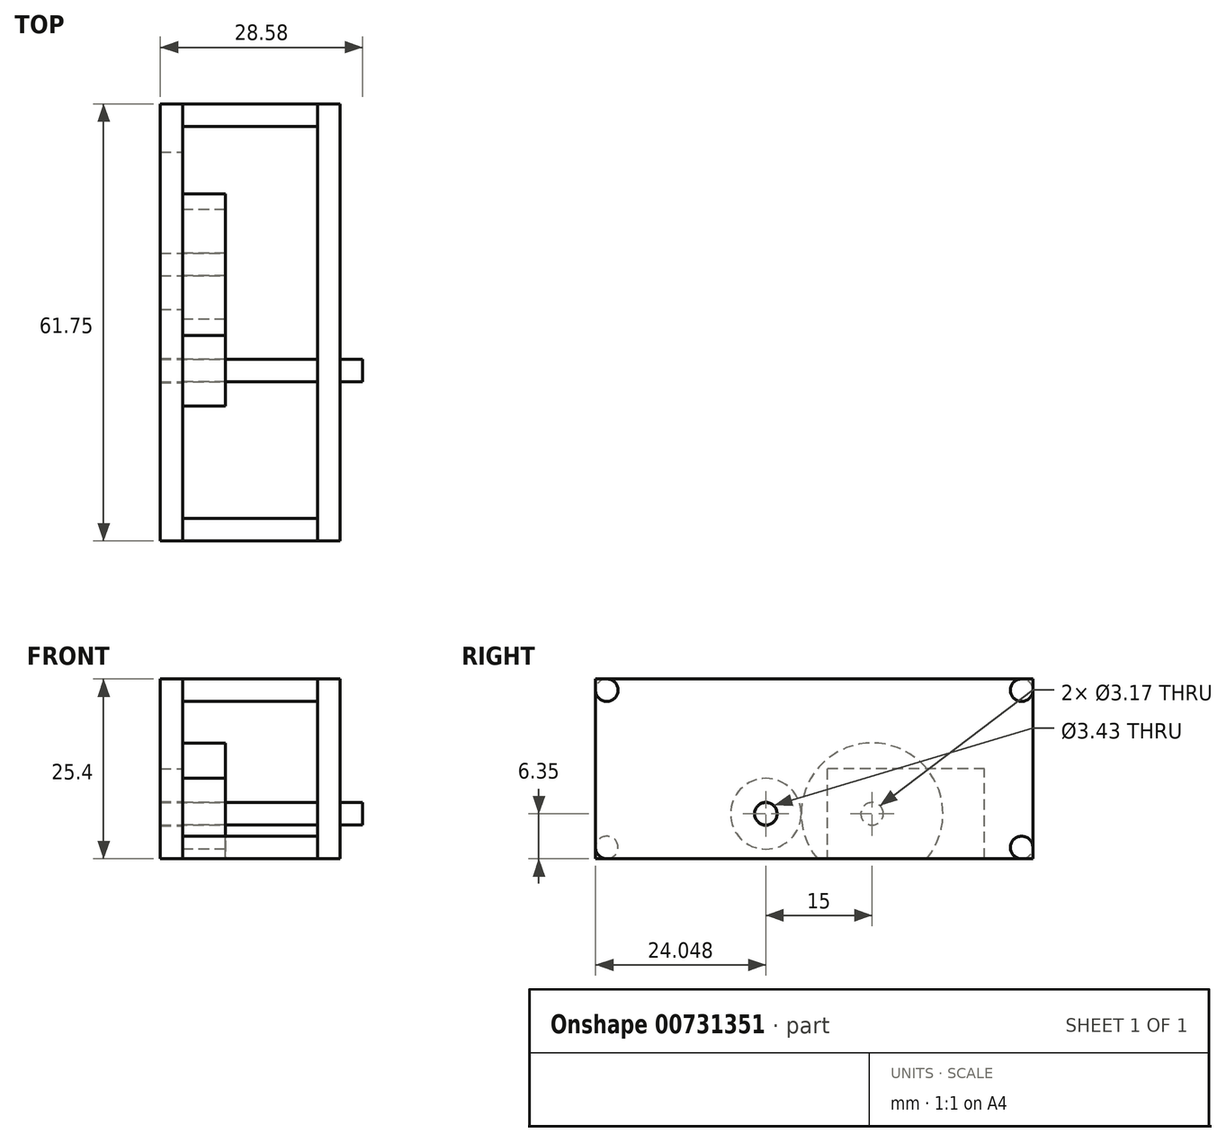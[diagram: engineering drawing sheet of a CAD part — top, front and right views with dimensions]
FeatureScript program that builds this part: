
annotation { "Feature Type Name" : "Feature", "Feature Type Description" : "" }
export const myFeature = defineFeature(function(context is Context, id is Id, definition is map)
    precondition{}
    {
        {
            var Q0;
            Q0=qCreatedBy(makeId("Right.planeOp"),FACE);
            var sketch = newSketch(context, id + "F0", { "sketchPlane" : qUnion([Q0])});
            skLineSegment(sketch, "E0", {"start": v(22.06, 6.35) * mm, "end": v(28.4, 6.35) * mm, "construction": true});
            skCircle(sketch, "E1", {"center": v(28.4, 6.35) * mm, "radius": 10 * mm});
            skLineSegment(sketch, "E2", {"start": v(28.4, 6.35) * mm, "end": v(13.4, 6.35) * mm, "construction": true});
            skCircle(sketch, "E3", {"center": v(13.4, 6.35) * mm, "radius": 5 * mm});
            skCircle(sketch, "E4", {"center": v(13.4, 6.35) * mm, "radius": 1.59 * mm});
            skCircle(sketch, "E5", {"center": v(28.4, 6.35) * mm, "radius": 1.59 * mm});
            skCircle(sketch, "E6", {"center": v(28.4, 6.35) * mm, "radius": 1.84 * mm});
            skLineSegment(sketch, "E7.bottom", {"start": v(35.82, 25.4) * mm, "end": v(51.1, 25.4) * mm});
            skLineSegment(sketch, "E7.top", {"start": v(43.49, 0) * mm, "end": v(51.1, 0) * mm});
            skLineSegment(sketch, "E7.right", {"start": v(51.1, 25.4) * mm, "end": v(51.1, 0) * mm});
            skLineSegment(sketch, "E8", {"start": v(8.4, 6.35) * mm, "end": v(-10.64, 6.35) * mm, "construction": true});
            skLineSegment(sketch, "E9", {"start": v(-10.64, 0) * mm, "end": v(-10.64, 25.4) * mm});
            skCircle(sketch, "E10", {"center": v(-9.05, 23.81) * mm, "radius": 1.59 * mm});
            skPoint(sketch, "E10.first.point", {"position": v(-9.05, 25.4) * mm});
            skPoint(sketch, "E10.second.point", {"position": v(-10.64, 23.81) * mm});
            skPoint(sketch, "E10.third.point", {"position": v(-8.61, 22.29) * mm});
            skCircle(sketch, "E11", {"center": v(-9.05, 1.59) * mm, "radius": 1.59 * mm});
            skPoint(sketch, "E11.first.point", {"position": v(-10.64, 1.59) * mm});
            skPoint(sketch, "E11.second.point", {"position": v(-9.05, 0) * mm});
            skPoint(sketch, "E11.third.point", {"position": v(-8.12, 2.87) * mm});
            skCircle(sketch, "E12", {"center": v(49.52, 1.59) * mm, "radius": 1.59 * mm});
            skPoint(sketch, "E12.first.point", {"position": v(49.52, 0) * mm});
            skPoint(sketch, "E12.second.point", {"position": v(51.1, 1.59) * mm});
            skPoint(sketch, "E12.third.point", {"position": v(47.96, 1.9) * mm});
            skCircle(sketch, "E13", {"center": v(49.52, 23.81) * mm, "radius": 1.59 * mm});
            skPoint(sketch, "E13.first.point", {"position": v(49.52, 25.4) * mm});
            skPoint(sketch, "E13.second.point", {"position": v(51.1, 23.81) * mm});
            skPoint(sketch, "E13.third.point", {"position": v(47.97, 23.48) * mm});
            skLineSegment(sketch, "E14.bottom", {"start": v(35.82, 25.4) * mm, "end": v(41.82, 25.4) * mm});
            skLineSegment(sketch, "E14.top", {"start": v(44.28, 0) * mm, "end": v(50.28, 0) * mm});
            skLineSegment(sketch, "E15", {"start": v(-10.64, 25.4) * mm, "end": v(35.82, 25.4) * mm});
            skLineSegment(sketch, "E16", {"start": v(44.28, 0) * mm, "end": v(44.28, 12.7) * mm});
            skLineSegment(sketch, "E17", {"start": v(44.28, 12.7) * mm, "end": v(22.06, 12.7) * mm});
            skPoint(sketch, "E17.endSnap0", {"position": v(22.06, 3.17) * mm});
            skLineSegment(sketch, "E18", {"start": v(22.06, 12.7) * mm, "end": v(22.06, 0) * mm});
            skLineSegment(sketch, "E19", {"start": v(-10.64, 0) * mm, "end": v(51.1, 0) * mm});
            skSolve(sketch);
        }
        {
            var Q0;
            {var subQ7=sQuery(id+"F0.wireOp",EDGE,"E3");Q0=makeQuery(id+"F0.imprint","IMPRINT",FACE,{"disambiguationData":[TD([[makeQuery(id+"F0.imprint","IMPRINT",EDGE,{"derivedFrom":subQ7}),-1.0]])]});}
            var Q1;
            {var subQ0=sQuery(id+"F0.wireOp",EDGE,"E7.right");var subQ1=sQuery(id+"F0.wireOp",EDGE,"E7.bottom");var subQ2=makeQuery(id+"F0.imprint","INTERSECT",VERTEX,{"derivedFrom":[subQ1,subQ0]});Q1=makeQuery(id+"F0.imprint","IMPRINT",FACE,{"disambiguationData":[TD([[makeQuery(id+"F0.imprint","IMPRINT",EDGE,{"disambiguationData":[TD([[subQ2,1.0]])],"derivedFrom":subQ1}),-1.0]])]});}
            var Q2;
            {var subQ0=sQuery(id+"F0.wireOp",EDGE,"E7.right");var subQ1=sQuery(id+"F0.wireOp",EDGE,"E7.top");var subQ2=makeQuery(id+"F0.imprint","INTERSECT",VERTEX,{"derivedFrom":[subQ1,subQ0]});Q2=makeQuery(id+"F0.imprint","IMPRINT",FACE,{"disambiguationData":[TD([[makeQuery(id+"F0.imprint","IMPRINT",EDGE,{"disambiguationData":[TD([[subQ2,1.0]])],"derivedFrom":subQ1}),1.0]])]});}
            var Q3;
            {var subQ0=sQuery(id+"F0.wireOp",EDGE,"E9");var subQ1=sQuery(id+"F0.wireOp",EDGE,"mzH20aDh-REpL-ww0y-ika9-ryDnuCNVRDq3");var subQ2=makeQuery(id+"F0.imprint","INTERSECT",VERTEX,{"derivedFrom":[subQ1,subQ0]});Q3=makeQuery(id+"F0.imprint","IMPRINT",FACE,{"disambiguationData":[TD([[makeQuery(id+"F0.imprint","IMPRINT",EDGE,{"disambiguationData":[TD([[subQ2,1.0]])],"derivedFrom":subQ1}),1.0]])]});}
            var Q4;
            {var subQ0=sQuery(id+"F0.wireOp",EDGE,"E9");var subQ1=sQuery(id+"F0.wireOp",EDGE,"AjtEDcku-NLsd-kfh1-AKqZ-MW7YpeOLVoxd");var subQ2=makeQuery(id+"F0.imprint","INTERSECT",VERTEX,{"derivedFrom":[subQ1,subQ0]});Q4=makeQuery(id+"F0.imprint","IMPRINT",FACE,{"disambiguationData":[TD([[makeQuery(id+"F0.imprint","IMPRINT",EDGE,{"disambiguationData":[TD([[subQ2,-1.0]])],"derivedFrom":subQ1}),1.0]])]});}
            var Q5;
            Q5=makeQuery(id+"F0.imprint","IMPRINT",FACE,{"disambiguationData":[TD([[makeQuery(id+"F0.imprint","IMPRINT",EDGE,{"derivedFrom":sQuery(id+"F0.wireOp",EDGE,"E3")}),1.0]])]});
            var Q6;
            {var subQ0=sQuery(id+"F0.wireOp",EDGE,"E13");var subQ1=makeQuery(id+"F0.imprint","INTERSECT",VERTEX,{"derivedFrom":[sQuery(id+"F0.wireOp",EDGE,"E7.bottom"),subQ0]});Q6=makeQuery(id+"F0.imprint","IMPRINT",FACE,{"disambiguationData":[TD([[makeQuery(id+"F0.imprint","IMPRINT",EDGE,{"disambiguationData":[TD([[subQ1,1.0]])],"derivedFrom":subQ0}),1.0]])]});}
            var Q7;
            {var subQ0=sQuery(id+"F0.wireOp",EDGE,"E12");var subQ1=makeQuery(id+"F0.imprint","INTERSECT",VERTEX,{"derivedFrom":[sQuery(id+"F0.wireOp",EDGE,"E7.top"),subQ0]});Q7=makeQuery(id+"F0.imprint","IMPRINT",FACE,{"disambiguationData":[TD([[makeQuery(id+"F0.imprint","IMPRINT",EDGE,{"disambiguationData":[TD([[subQ1,1.0]])],"derivedFrom":subQ0}),1.0]])]});}
            var Q8;
            {var subQ0=sQuery(id+"F0.wireOp",EDGE,"E11");var subQ1=makeQuery(id+"F0.imprint","INTERSECT",VERTEX,{"derivedFrom":[sQuery(id+"F0.wireOp",EDGE,"AjtEDcku-NLsd-kfh1-AKqZ-MW7YpeOLVoxd"),subQ0]});Q8=makeQuery(id+"F0.imprint","IMPRINT",FACE,{"disambiguationData":[TD([[makeQuery(id+"F0.imprint","IMPRINT",EDGE,{"disambiguationData":[TD([[subQ1,1.0]])],"derivedFrom":subQ0}),1.0]])]});}
            var Q9;
            {var subQ0=sQuery(id+"F0.wireOp",EDGE,"E10");var subQ1=makeQuery(id+"F0.imprint","INTERSECT",VERTEX,{"derivedFrom":[sQuery(id+"F0.wireOp",EDGE,"mzH20aDh-REpL-ww0y-ika9-ryDnuCNVRDq3"),subQ0]});Q9=makeQuery(id+"F0.imprint","IMPRINT",FACE,{"disambiguationData":[TD([[makeQuery(id+"F0.imprint","IMPRINT",EDGE,{"disambiguationData":[TD([[subQ1,-1.0]])],"derivedFrom":subQ0}),1.0]])]});}
            var Q10;
            {var subQ0=sQuery(id+"F0.wireOp",EDGE,"E13");var subQ1=sQuery(id+"F0.wireOp",EDGE,"E7.right");var subQ2=makeQuery(id+"F0.imprint","INTERSECT",VERTEX,{"derivedFrom":[subQ1,subQ0]});Q10=makeQuery(id+"F0.imprint","IMPRINT",FACE,{"disambiguationData":[TD([[makeQuery(id+"F0.imprint","IMPRINT",EDGE,{"disambiguationData":[TD([[subQ2,-1.0]])],"derivedFrom":subQ1}),-1.0]])]});}
            var Q11;
            {var subQ0=sQuery(id+"F0.wireOp",EDGE,"E14.top");var subQ1=sQuery(id+"F0.wireOp",EDGE,"E12");var subQ2=makeQuery(id+"F0.imprint","INTERSECT",VERTEX,{"derivedFrom":[subQ1,subQ0]});Q11=makeQuery(id+"F0.imprint","IMPRINT",FACE,{"disambiguationData":[TD([[makeQuery(id+"F0.imprint","IMPRINT",EDGE,{"disambiguationData":[TD([[subQ2,1.0]])],"derivedFrom":subQ1}),-1.0]])]});}
            var Q12;
            {var subQ0=sQuery(id+"F0.wireOp",EDGE,"E14.top");var subQ1=sQuery(id+"F0.wireOp",EDGE,"E7.right");var subQ2=makeQuery(id+"F0.imprint","INTERSECT",VERTEX,{"derivedFrom":[subQ1,subQ0]});Q12=makeQuery(id+"F0.imprint","IMPRINT",FACE,{"disambiguationData":[TD([[makeQuery(id+"F0.imprint","IMPRINT",EDGE,{"disambiguationData":[TD([[subQ2,1.0]])],"derivedFrom":subQ1}),-1.0]])]});}
            var Q13;
            {var subQ0=sQuery(id+"F0.wireOp",EDGE,"E14.bottom");var subQ1=sQuery(id+"F0.wireOp",EDGE,"E13");var subQ2=makeQuery(id+"F0.imprint","INTERSECT",VERTEX,{"derivedFrom":[subQ1,subQ0]});Q13=makeQuery(id+"F0.imprint","IMPRINT",FACE,{"disambiguationData":[TD([[makeQuery(id+"F0.imprint","IMPRINT",EDGE,{"disambiguationData":[TD([[subQ2,-1.0]])],"derivedFrom":subQ1}),-1.0]])]});}
            var Q14;
            {var subQ0=sQuery(id+"F0.wireOp",EDGE,"E14.bottom");var subQ1=sQuery(id+"F0.wireOp",EDGE,"E7.right");var subQ2=makeQuery(id+"F0.imprint","INTERSECT",VERTEX,{"derivedFrom":[subQ1,subQ0]});Q14=makeQuery(id+"F0.imprint","IMPRINT",FACE,{"disambiguationData":[TD([[makeQuery(id+"F0.imprint","IMPRINT",EDGE,{"disambiguationData":[TD([[subQ2,-1.0]])],"derivedFrom":subQ1}),-1.0]])]});}
            var Q15;
            {var subQ0=sQuery(id+"F0.wireOp",EDGE,"E15");var subQ1=sQuery(id+"F0.wireOp",EDGE,"E9");var subQ2=makeQuery(id+"F0.imprint","INTERSECT",VERTEX,{"derivedFrom":[subQ1,subQ0]});Q15=makeQuery(id+"F0.imprint","IMPRINT",FACE,{"disambiguationData":[TD([[makeQuery(id+"F0.imprint","IMPRINT",EDGE,{"disambiguationData":[TD([[subQ2,1.0]])],"derivedFrom":subQ1}),-1.0]])]});}
            var Q16;
            {var subQ0=sQuery(id+"F0.wireOp",EDGE,"E18");Q16=makeQuery(id+"F0.imprint","IMPRINT",FACE,{"disambiguationData":[TD([[makeQuery(id+"F0.imprint","IMPRINT",EDGE,{"derivedFrom":subQ0}),-1.0]])]});}
            var Q17;
            {var subQ0=sQuery(id+"F0.wireOp",EDGE,"E16");Q17=makeQuery(id+"F0.imprint","IMPRINT",FACE,{"disambiguationData":[TD([[makeQuery(id+"F0.imprint","IMPRINT",EDGE,{"derivedFrom":subQ0}),1.0]])]});}
            var Q18;
            Q18=makeQuery(id+"F0.imprint","IMPRINT",FACE,{"disambiguationData":[TD([[makeQuery(id+"F0.imprint","IMPRINT",EDGE,{"derivedFrom":sQuery(id+"F0.wireOp",EDGE,"E6")}),-1.0]])]});
            var Q19;
            Q19=makeQuery(id+"F0.imprint","IMPRINT",FACE,{"disambiguationData":[TD([[makeQuery(id+"F0.imprint","IMPRINT",EDGE,{"derivedFrom":sQuery(id+"F0.wireOp",EDGE,"E5")}),1.0]])]});
            var Q20;
            Q20=makeQuery(id+"F0.imprint","IMPRINT",FACE,{"disambiguationData":[TD([[makeQuery(id+"F0.imprint","IMPRINT",EDGE,{"derivedFrom":sQuery(id+"F0.wireOp",EDGE,"E5")}),-1.0]])]});
            var Q21;
            {var subQ0=sQuery(id+"F0.wireOp",EDGE,"E19");var subQ1=sQuery(id+"F0.wireOp",EDGE,"E9");var subQ2=makeQuery(id+"F0.imprint","INTERSECT",VERTEX,{"derivedFrom":[subQ1,subQ0]});Q21=makeQuery(id+"F0.imprint","IMPRINT",FACE,{"disambiguationData":[TD([[makeQuery(id+"F0.imprint","IMPRINT",EDGE,{"disambiguationData":[TD([[subQ2,-1.0]])],"derivedFrom":subQ1}),-1.0]])]});}
            extrude(context, id + "F1", {"entities" : qUnion([Q0, Q1, Q2, Q3, Q4, Q5, Q6, Q7, Q8, Q9, Q10, Q11, Q12, Q13, Q14, Q15, Q16, Q17, Q18, Q19, Q20, Q21]), "depth" : 3.17 * mm, "offsetDistance" : 25.4 * mm});
        }
        {
            var Q0;
            {var subQ0=sQuery(id+"F0.wireOp",EDGE,"E13");var subQ1=makeQuery(id+"F0.imprint","INTERSECT",VERTEX,{"derivedFrom":[sQuery(id+"F0.wireOp",EDGE,"E7.bottom"),subQ0]});Q0=makeQuery(id+"F0.imprint","IMPRINT",FACE,{"disambiguationData":[TD([[makeQuery(id+"F0.imprint","IMPRINT",EDGE,{"disambiguationData":[TD([[subQ1,1.0]])],"derivedFrom":subQ0}),1.0]])]});}
            var Q1;
            {var subQ0=sQuery(id+"F0.wireOp",EDGE,"E12");var subQ1=makeQuery(id+"F0.imprint","INTERSECT",VERTEX,{"derivedFrom":[sQuery(id+"F0.wireOp",EDGE,"E7.top"),subQ0]});Q1=makeQuery(id+"F0.imprint","IMPRINT",FACE,{"disambiguationData":[TD([[makeQuery(id+"F0.imprint","IMPRINT",EDGE,{"disambiguationData":[TD([[subQ1,1.0]])],"derivedFrom":subQ0}),1.0]])]});}
            var Q2;
            {var subQ0=sQuery(id+"F0.wireOp",EDGE,"E11");var subQ1=makeQuery(id+"F0.imprint","INTERSECT",VERTEX,{"derivedFrom":[sQuery(id+"F0.wireOp",EDGE,"AjtEDcku-NLsd-kfh1-AKqZ-MW7YpeOLVoxd"),subQ0]});Q2=makeQuery(id+"F0.imprint","IMPRINT",FACE,{"disambiguationData":[TD([[makeQuery(id+"F0.imprint","IMPRINT",EDGE,{"disambiguationData":[TD([[subQ1,1.0]])],"derivedFrom":subQ0}),1.0]])]});}
            var Q3;
            {var subQ0=sQuery(id+"F0.wireOp",EDGE,"E10");var subQ1=makeQuery(id+"F0.imprint","INTERSECT",VERTEX,{"derivedFrom":[sQuery(id+"F0.wireOp",EDGE,"mzH20aDh-REpL-ww0y-ika9-ryDnuCNVRDq3"),subQ0]});Q3=makeQuery(id+"F0.imprint","IMPRINT",FACE,{"disambiguationData":[TD([[makeQuery(id+"F0.imprint","IMPRINT",EDGE,{"disambiguationData":[TD([[subQ1,-1.0]])],"derivedFrom":subQ0}),1.0]])]});}
            extrude(context, id + "F2", {"entities" : qUnion([Q0, Q1, Q2, Q3]), "oppositeDirection" : true, "depth" : 19.05 * mm, "offsetDistance" : 25.4 * mm});
        }
        {
            var Q0;
            Q0=makeQuery(id+"F2.opExtrude","CAP_FACE",FACE,{"disambiguationData":[OSD([sQuery(id+"F0.wireOp",EDGE,"E13")])],"isStart":false});
            var sketch = newSketch(context, id + "F3", { "sketchPlane" : qUnion([Q0])});
            skLineSegment(sketch, "E20.bottom", {"start": v(-51.1, 25.4) * mm, "end": v(10.64, 25.4) * mm});
            skLineSegment(sketch, "E20.top", {"start": v(-51.1, 0) * mm, "end": v(10.64, 0) * mm});
            skLineSegment(sketch, "E20.left", {"start": v(-51.1, 25.4) * mm, "end": v(-51.1, 0) * mm});
            skLineSegment(sketch, "E20.right", {"start": v(10.64, 25.4) * mm, "end": v(10.64, 0) * mm});
            skLineSegment(sketch, "E21", {"start": v(-44.28, 6.35) * mm, "end": v(-44.28, 0) * mm, "construction": true});
            skLineSegment(sketch, "E22", {"start": v(-44.28, 6.35) * mm, "end": v(-22.06, 6.35) * mm, "construction": true});
            skLineSegment(sketch, "E23", {"start": v(-22.06, 6.35) * mm, "end": v(-22.06, 0) * mm, "construction": true});
            skLineSegment(sketch, "E24", {"start": v(-22.06, 6.35) * mm, "end": v(-28.4, 6.35) * mm});
            skCircle(sketch, "E25", {"center": v(-28.4, 6.35) * mm, "radius": 10 * mm});
            skLineSegment(sketch, "E26", {"start": v(-28.4, 6.35) * mm, "end": v(-13.4, 6.35) * mm, "construction": true});
            skCircle(sketch, "E27", {"center": v(-13.4, 6.35) * mm, "radius": 5 * mm});
            skCircle(sketch, "E28", {"center": v(-13.4, 6.35) * mm, "radius": 1.59 * mm});
            skCircle(sketch, "E29", {"center": v(-13.4, 6.35) * mm, "radius": 1.71 * mm});
            skCircle(sketch, "E30", {"center": v(-28.4, 6.35) * mm, "radius": 1.84 * mm});
            skCircle(sketch, "E31", {"center": v(-28.4, 6.35) * mm, "radius": 1.59 * mm});
            skLineSegment(sketch, "E32", {"start": v(-44.28, 0) * mm, "end": v(-44.28, 12.7) * mm});
            skLineSegment(sketch, "E33", {"start": v(-44.28, 12.7) * mm, "end": v(-22.06, 12.7) * mm});
            skLineSegment(sketch, "E34", {"start": v(-22.06, 12.7) * mm, "end": v(-22.06, 0) * mm});
            skSolve(sketch);
        }
        {
            var Q0;
            {var subQ0=sQuery(id+"F3.wireOp",EDGE,"61rDZBB9-DkLB-R1jF-Ugw1-9J4s0qTPQNlm");var subQ1=sQuery(id+"F3.wireOp",EDGE,"E20.top");var subQ2=makeQuery(id+"F3.imprint","INTERSECT",VERTEX,{"disambiguationData":[OD(0.0)],"derivedFrom":[subQ1,subQ0]});Q0=makeQuery(id+"F3.imprint","IMPRINT",FACE,{"disambiguationData":[TD([[makeQuery(id+"F3.imprint","IMPRINT",EDGE,{"disambiguationData":[TD([[subQ2,-1.0]])],"derivedFrom":subQ1}),1.0]])]});}
            var Q1;
            Q1=makeQuery(id+"F3.imprint","IMPRINT",FACE,{"disambiguationData":[TD([[makeQuery(id+"F3.imprint","IMPRINT",EDGE,{"derivedFrom":sQuery(id+"F3.wireOp",EDGE,"f6RzX2im-ddRW-lgic-JvNA-CsLhbOmZ7d9f")}),1.0]])]});
            var Q2;
            {var subQ0=sQuery(id+"F3.wireOp",EDGE,"E20.right");Q2=makeQuery(id+"F3.imprint","IMPRINT",FACE,{"disambiguationData":[TD([[makeQuery(id+"F3.imprint","IMPRINT",EDGE,{"derivedFrom":subQ0}),-1.0]])]});}
            var Q3;
            {var subQ0=sQuery(id+"F3.wireOp",EDGE,"E20.left");var subQ1=sQuery(id+"F3.wireOp",EDGE,"E20.bottom");var subQ2=makeQuery(id+"F3.imprint","INTERSECT",VERTEX,{"derivedFrom":[subQ1,subQ0]});Q3=makeQuery(id+"F3.imprint","IMPRINT",FACE,{"disambiguationData":[TD([[makeQuery(id+"F3.imprint","IMPRINT",EDGE,{"disambiguationData":[TD([[subQ2,-1.0]])],"derivedFrom":subQ1}),-1.0]])]});}
            var Q4;
            {var subQ0=makeQuery(id+"F2.opExtrude","CAP_EDGE",EDGE,{"disambiguationData":[OSD([sQuery(id+"F0.wireOp",EDGE,"E13")])],"isStart":false});var subQ1=makeQuery(id+"F3.imprint","INTERSECT",VERTEX,{"derivedFrom":[subQ0,sQuery(id+"F3.wireOp",EDGE,"E20.bottom")]});Q4=makeQuery(id+"F3.imprint","IMPRINT",FACE,{"disambiguationData":[TD([[makeQuery(id+"F3.imprint","IMPRINT",EDGE,{"disambiguationData":[TD([[subQ1,1.0]])],"derivedFrom":subQ0}),-1.0]])]});}
            var Q5;
            Q5=makeQuery(id+"F3.imprint","IMPRINT",FACE,{"disambiguationData":[TD([[makeQuery(id+"F3.imprint","IMPRINT",EDGE,{"derivedFrom":sQuery(id+"F3.wireOp",EDGE,"E27")}),1.0]])]});
            var Q6;
            {var subQ0=sQuery(id+"F3.wireOp",EDGE,"E34");var subQ9=makeQuery(id+"F3.imprint","IMPRINT",VERTEX,{"derivedFrom":subQ0});Q6=makeQuery(id+"F3.imprint","IMPRINT",FACE,{"disambiguationData":[TD([[makeQuery(id+"F3.imprint","IMPRINT",EDGE,{"disambiguationData":[TD([[subQ9,1.0]])],"derivedFrom":subQ0}),1.0]])]});}
            extrude(context, id + "F4", {"entities" : qUnion([Q0, Q1, Q2, Q3, Q4, Q5, Q6]), "operationType" : NewBodyOperationType.ADD, "depth" : 3.17 * mm, "offsetDistance" : 25.4 * mm});
        }
        {
            var Q0;
            Q0=makeQuery(id+"F3.imprint","IMPRINT",FACE,{"disambiguationData":[TD([[makeQuery(id+"F3.imprint","IMPRINT",EDGE,{"derivedFrom":sQuery(id+"F3.wireOp",EDGE,"E31")}),1.0]])]});
            extrude(context, id + "F5", {"entities" : qUnion([Q0]), "depth" : 3.17 * mm, "offsetDistance" : 25.4 * mm});
        }
        {
            var Q0;
            Q0=makeQuery(id+"F3.imprint","IMPRINT",FACE,{"disambiguationData":[TD([[makeQuery(id+"F3.imprint","IMPRINT",EDGE,{"derivedFrom":sQuery(id+"F3.wireOp",EDGE,"E31")}),1.0]])]});
            extrude(context, id + "F6", {"entities" : qUnion([Q0]), "operationType" : NewBodyOperationType.ADD, "oppositeDirection" : true, "depth" : 6 * mm, "offsetDistance" : 25.4 * mm});
        }
        {
            var Q0;
            {var subQ0=sQuery(id+"F3.wireOp",EDGE,"E25");var subQ1=sQuery(id+"F3.wireOp",EDGE,"E20.top");var subQ2=makeQuery(id+"F3.imprint","INTERSECT",VERTEX,{"disambiguationData":[OD(0.0)],"derivedFrom":[subQ1,subQ0]});Q0=makeQuery(id+"F3.imprint","IMPRINT",FACE,{"disambiguationData":[TD([[makeQuery(id+"F3.imprint","IMPRINT",EDGE,{"disambiguationData":[TD([[subQ2,-1.0]])],"derivedFrom":subQ1}),-1.0]])]});}
            var Q1;
            Q1=makeQuery(id+"F3.imprint","IMPRINT",FACE,{"disambiguationData":[TD([[makeQuery(id+"F3.imprint","IMPRINT",EDGE,{"derivedFrom":sQuery(id+"F3.wireOp",EDGE,"E30")}),-1.0]])]});
            var Q2;
            Q2=makeQuery(id+"F3.imprint","IMPRINT",FACE,{"disambiguationData":[TD([[makeQuery(id+"F3.imprint","IMPRINT",EDGE,{"derivedFrom":sQuery(id+"F3.wireOp",EDGE,"E30")}),1.0]])]});
            var Q3;
            {var subQ0=sQuery(id+"F3.wireOp",EDGE,"E34");var subQ9=makeQuery(id+"F3.imprint","IMPRINT",VERTEX,{"derivedFrom":subQ0});Q3=makeQuery(id+"F3.imprint","IMPRINT",FACE,{"disambiguationData":[TD([[makeQuery(id+"F3.imprint","IMPRINT",EDGE,{"disambiguationData":[TD([[subQ9,1.0]])],"derivedFrom":subQ0}),1.0]])]});}
            extrude(context, id + "F7", {"entities" : qUnion([Q0, Q1, Q2, Q3]), "oppositeDirection" : true, "depth" : 6 * mm, "offsetDistance" : 25.4 * mm});
        }
        {
            var Q0;
            Q0=makeQuery(id+"F3.imprint","IMPRINT",FACE,{"disambiguationData":[TD([[makeQuery(id+"F3.imprint","IMPRINT",EDGE,{"derivedFrom":sQuery(id+"F3.wireOp",EDGE,"E28")}),1.0]])]});
            extrude(context, id + "F8", {"entities" : qUnion([Q0]), "depth" : 3.17 * mm, "offsetDistance" : 25.4 * mm});
        }
        {
            var Q0;
            Q0=makeQuery(id+"F3.imprint","IMPRINT",FACE,{"disambiguationData":[TD([[makeQuery(id+"F3.imprint","IMPRINT",EDGE,{"derivedFrom":sQuery(id+"F3.wireOp",EDGE,"E28")}),1.0]])]});
            extrude(context, id + "F9", {"entities" : qUnion([Q0]), "operationType" : NewBodyOperationType.ADD, "oppositeDirection" : true, "depth" : 25.4 * mm, "offsetDistance" : 25.4 * mm});
        }
        {
            var Q0;
            Q0=makeQuery(id+"F3.imprint","IMPRINT",FACE,{"disambiguationData":[TD([[makeQuery(id+"F3.imprint","IMPRINT",EDGE,{"derivedFrom":sQuery(id+"F3.wireOp",EDGE,"E27")}),1.0]])]});
            var Q1;
            Q1=makeQuery(id+"F3.imprint","IMPRINT",FACE,{"disambiguationData":[TD([[makeQuery(id+"F3.imprint","IMPRINT",EDGE,{"derivedFrom":sQuery(id+"F3.wireOp",EDGE,"E28")}),-1.0]])]});
            extrude(context, id + "F10", {"entities" : qUnion([Q0, Q1]), "oppositeDirection" : true, "depth" : 6 * mm, "offsetDistance" : 25.4 * mm});
        }
    });
